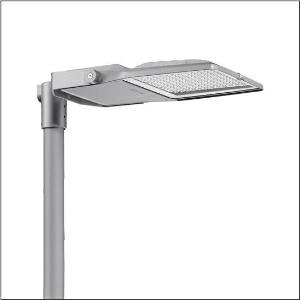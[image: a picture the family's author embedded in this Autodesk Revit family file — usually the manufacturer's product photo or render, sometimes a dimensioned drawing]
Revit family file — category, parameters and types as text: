
# Revit family: floodlight_fl_21_iq_midi___pl52_5xa7782e4d3a_8c54
name_source: partatom
category: Lighting Fixtures
units: mm (PartAtom-declared; Revit-internal decimal feet)

## family parameters
Cut with Voids When Loaded = No
Host = Face
Light Source = No
Part Type = Normal
Room Calculation Point = No
Round Connector Dimension = Use Diameter
Shared = No

## types (1)
- --- (1 x LED, 28010 lm, 208.1 W, 4000K)
    Apparent Load = 208 VA
    CIE Flux Codes = 26 60 98 100 100
    Color Rendering = 70
    Color Temperature = 4000K
    Default Elevation = 1800 mm
    Description = Floodlight FL 21 iQ midi, floodlight, primary light control with lens, of PMMA, primary optical cover: protective disc, of toughened safety glass, transparent, light distribution: PL52, light emission: direct distribution, installation type: surface-mounted, lamps: LED, High Power LED, rated values: 28.010lm | 208,1W | 134,6lm/W (begin service life); end service life: 28.010lm | 227,1W; at 50% lumin. flux: 14.005lm | 90,3W | 155,1lm/W, colour temperature: 4000K, colour rendering: CRI > 70, light colour: 740, light setting 1 begin service life: 100% | 28.010lm | 208,1W | 134,6lm/W | 4.000K, light setting 1 end service life: 227,1W, further light settings possible, control: optimised constant luminous flux control (CLO 2.0), Desk-Remote (wireless, voltage-free reading and setting of iQ features in the workshop via application-optimized NFC function/RFID function), Smart-Wire, Night-Set, Temp-Guard, Auto-Match, Street-Remote, pre-setting: linear dimming characteristic, with terminal, 6-pole, mains connection: 220..240V, AC, 50/60Hz, luminaire housing, of diecast aluminium, powder-coated, SITECO metallic grey (DB 702S), corrosivity category C5 mid according to DIN EN ISO 12944suitable for swimming poolschlorine-resistant, sealing non-destructively replaceable, please order mast flange separately, mast bracket, of steel, galvanised, powder-coated, SITECO metallic grey (DB 702S), protection rating (complete): IP66, insulation class (complete): insulation class II (safety insulation), certification: CE, ENEC, VDE, protection symbol: D, impact resistance: IK08, permissible operating ambient temperature: -40..+40°C, permissible operating ambient temperature for outdoor applications: -40..+50°C, standard: DIN EN 12944, LABS conformity tested according to VDMA 24364:2018-05, packaging unit: 1 piece

Light Distribution: PL52
    Height = 76 mm
    Lamp = 1 x LED
    Lamp Light Flux = 28010 lm
    Lamp Power = 208.1 W
    Lamp count = 1
    Length = 657 mm
    Luminous efficacy = 135 lm/W
    Manufacturer = Siteco
    ModVariant = No
    Model = 5XA7782E4D3A
    Mounting Place = Pole
    Mounting Type = Pole annexe
    Number of Poles = 1
    OnlyDefault = Yes
    Power Factor = 1
    Product Name = Floodlight FL 21 iQ midi | PL52
    Product group = floodlight | pylon annexe
    ProductGroupID = 6201
    Protection Class = Protection class II
    Protection Degree = IP 66
    RLX_Detail_Level = 1
    RLX_Emergency_Light_Flux = 0 lm
    RLX_Emergency_Type = 0
    RLX_Emergency_Type_DB = No
    RlxData = <blob elided: 153929 chars, md5=428c09e8>
    Socket = socket
    Standby Power = 0 W
    System Light Flux = 28010 lm
    System Power = 208 W
    Type Comments = factory setting: luminous flux: 100 % | dim-lin: 254 | 710 mA
    Type Image = l_1007123.jpg
    URL = http://relux.com
    VarID = @adj_107473
    Voltage = 0 V
    Weight = 0.00 kg
    Width = 442 mm

## geometry (parser evidence)
native form markers: Blend x4, Sweep x14
no freeform markers — native parametric forms only
